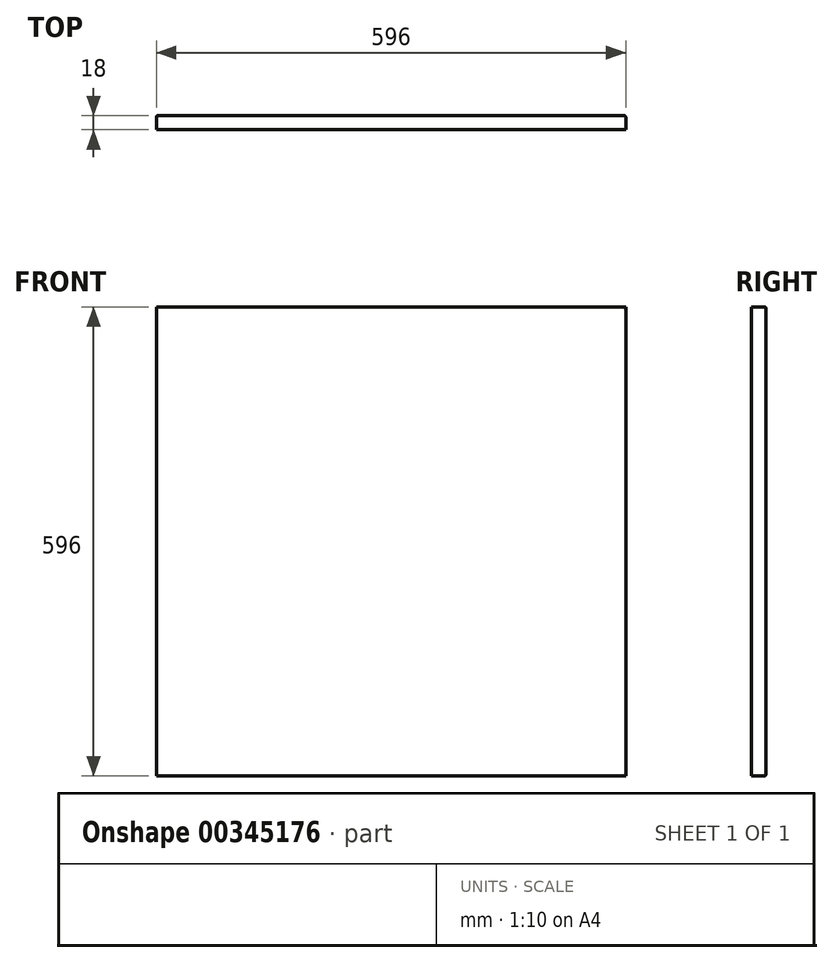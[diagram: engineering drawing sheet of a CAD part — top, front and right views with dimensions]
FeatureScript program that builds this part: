
annotation { "Feature Type Name" : "Feature", "Feature Type Description" : "" }
export const myFeature = defineFeature(function(context is Context, id is Id, definition is map)
    precondition{}
    {
        {
            var Q0;
            Q0=qCreatedBy(makeId("Front.planeOp"),FACE);
            var sketch = newSketch(context, id + "F0", { "sketchPlane" : qUnion([Q0])});
            skLineSegment(sketch, "E0.bottom", {"start": v(0, 0) * mm, "end": v(-60.98, 0) * mm});
            skLineSegment(sketch, "E0.top", {"start": v(0, 42.94) * mm, "end": v(-60.98, 42.94) * mm});
            skLineSegment(sketch, "E0.left", {"start": v(0, 0) * mm, "end": v(0, 42.94) * mm});
            skLineSegment(sketch, "E0.right", {"start": v(-60.98, 0) * mm, "end": v(-60.98, 42.94) * mm});
            skSolve(sketch);
        }
        {
            var Q0;
            Q0=makeQuery(id+"F0.imprint","IMPRINT",FACE,{"disambiguationData":[TD([[makeQuery(id+"F0.imprint","IMPRINT",EDGE,{"derivedFrom":sQuery(id+"F0.wireOp",EDGE,"E0.bottom")}),-1.0]])]});
            extrude(context, id + "F1", {"entities" : qUnion([Q0]), "oppositeDirection" : true, "depth" : 18 * mm});
        }
        {
            var Q0;
            Q0=makeQuery(id+"F1.opExtrude","SWEPT_FACE",FACE,{"disambiguationData":[OSD([sQuery(id+"F0.wireOp",EDGE,"E0.left")])]});
            extrude(context, id + "F2", {"entities" : qUnion([Q0]), "operationType" : NewBodyOperationType.ADD, "oppositeDirection" : true, "depth" : 596 * mm});
        }
        {
            var Q0;
            {var subQ0=sQuery(id+"F0.wireOp",EDGE,"E0.bottom");Q0=makeQuery(id+"F2.boolean.opBoolean","MERGE",FACE,{"derivedFrom":[makeQuery(id+"F1.opExtrude","SWEPT_FACE",FACE,{"disambiguationData":[OSD([subQ0])]}),makeQuery(id+"F2.opExtrude","SWEPT_FACE",FACE,{"disambiguationData":[OSD([subQ0,sQuery(id+"F0.wireOp",EDGE,"E0.left")])]})]});}
            extrude(context, id + "F3", {"entities" : qUnion([Q0]), "operationType" : NewBodyOperationType.ADD, "oppositeDirection" : true, "depth" : 596 * mm});
        }
        {
            var Q0;
            {var subQ0=sQuery(id+"F0.wireOp",EDGE,"E0.left");var subQ1=sQuery(id+"F0.wireOp",EDGE,"E0.bottom");Q0=makeQuery(id+"F3.boolean.opBoolean","MERGE",FACE,{"derivedFrom":[makeQuery(id+"F2.boolean.opBoolean","MERGE",FACE,{"derivedFrom":[makeQuery(id+"F1.opExtrude","CAP_FACE",FACE,{"disambiguationData":[OSD([subQ1,sQuery(id+"F0.wireOp",EDGE,"E0.top"),subQ0,sQuery(id+"F0.wireOp",EDGE,"E0.right")])],"isStart":false}),makeQuery(id+"F2.opExtrude","SWEPT_FACE",FACE,{"disambiguationData":[OSD([subQ0]),TDD([makeQuery(id+"F1.opExtrude","CAP_EDGE",EDGE,{"disambiguationData":[OSD([subQ0])],"isStart":false})])]})]}),makeQuery(id+"F3.opExtrude","SWEPT_FACE",FACE,{"disambiguationData":[OSD([subQ1,subQ0]),TDD([makeQuery(id+"F2.boolean.opBoolean","MERGE",EDGE,{"derivedFrom":[makeQuery(id+"F1.opExtrude","CAP_EDGE",EDGE,{"disambiguationData":[OSD([subQ1])],"isStart":false}),makeQuery(id+"F2.opExtrude","SWEPT_EDGE",EDGE,{"disambiguationData":[OSD([subQ1,subQ0]),TDD([makeQuery(id+"F1.opExtrude","CAP_VERTEX",VERTEX,{"disambiguationData":[OSD([subQ1,subQ0])],"isStart":false})])]})]})])]})]});}
            fillet(context, id + "F4", {"entities" : qUnion([Q0]), "radius" : 2 * mm, "tangentPropagation" : true, "allowEdgeOverflow" : false});
        }
    });
